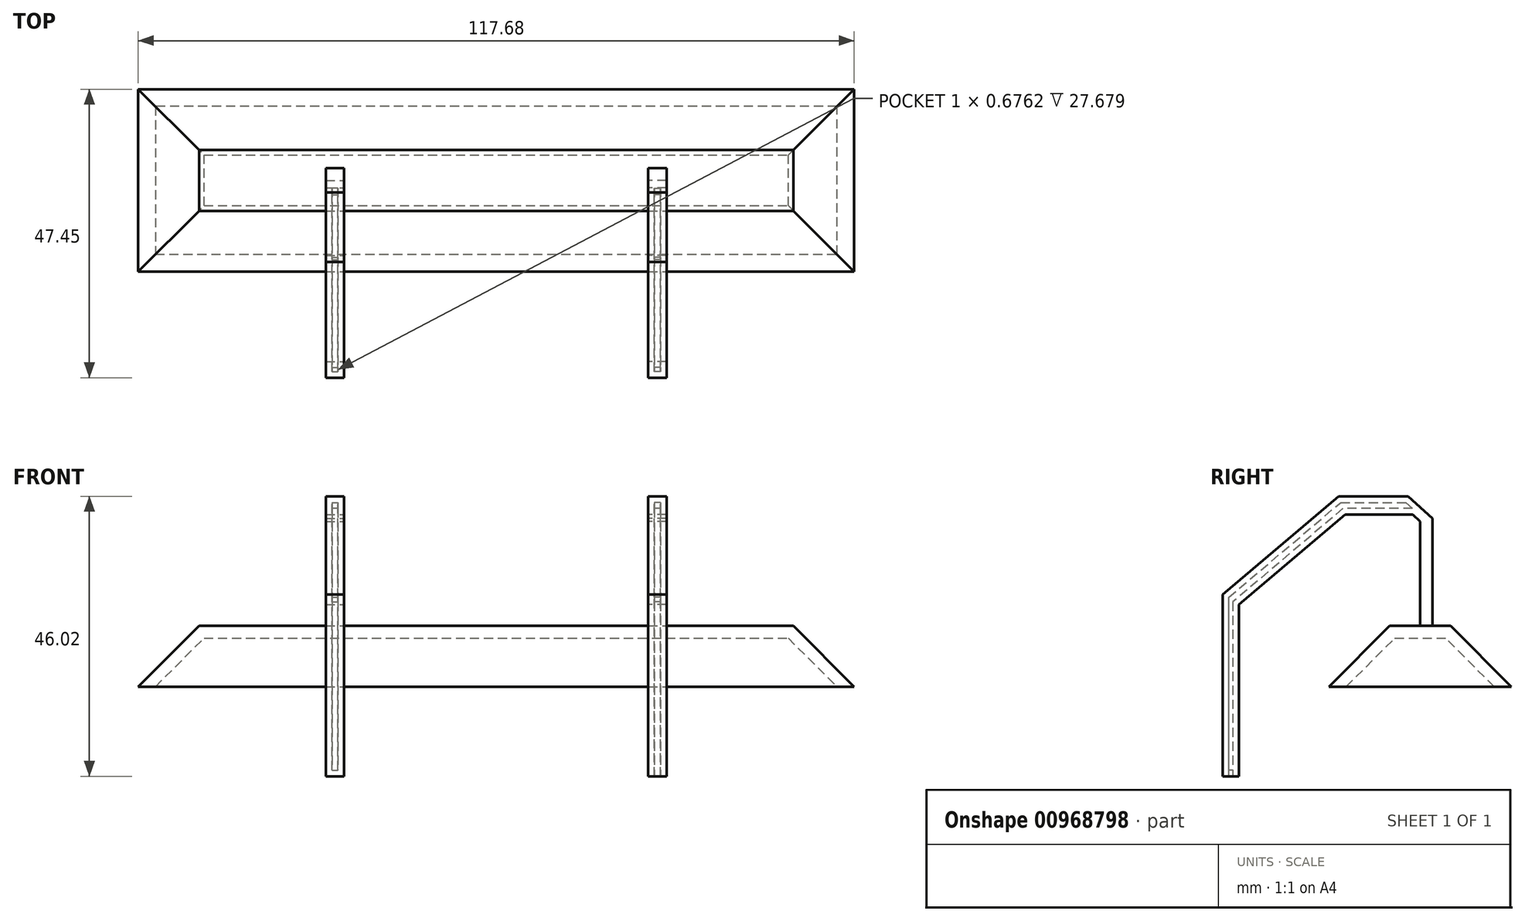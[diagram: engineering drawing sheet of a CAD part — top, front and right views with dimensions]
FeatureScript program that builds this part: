
annotation { "Feature Type Name" : "Feature", "Feature Type Description" : "" }
export const myFeature = defineFeature(function(context is Context, id is Id, definition is map)
    precondition{}
    {
        {
            var Q0;
            Q0=qCreatedBy(makeId("Top.planeOp"),FACE);
            var sketch = newSketch(context, id + "F0", { "sketchPlane" : qUnion([Q0])});
            skLineSegment(sketch, "E0.bottom", {"start": v(-0.04, 0) * mm, "end": v(117.64, 0) * mm});
            skLineSegment(sketch, "E0.top", {"start": v(-0.04, 30) * mm, "end": v(117.64, 30) * mm});
            skLineSegment(sketch, "E0.left", {"start": v(-0.04, 0) * mm, "end": v(-0.04, 30) * mm});
            skLineSegment(sketch, "E0.right", {"start": v(117.64, 0) * mm, "end": v(117.64, 30) * mm});
            skSolve(sketch);
        }
        {
            var Q0;
            Q0 = qSketchRegion(id + "F0", true);
            extrude(context, id + "F1", {"entities" : qUnion([Q0]), "depth" : 10 * mm, "offsetDistance" : 25 * mm});
        }
        {
            var Q0;
            Q0=makeQuery(id+"F1.opExtrude","CAP_EDGE",EDGE,{"disambiguationData":[OSD([sQuery(id+"F0.wireOp",EDGE,"E0.bottom")])],"isStart":false});
            var Q1;
            Q1=makeQuery(id+"F1.opExtrude","CAP_EDGE",EDGE,{"disambiguationData":[OSD([sQuery(id+"F0.wireOp",EDGE,"E0.right")])],"isStart":false});
            var Q2;
            Q2=makeQuery(id+"F1.opExtrude","CAP_EDGE",EDGE,{"disambiguationData":[OSD([sQuery(id+"F0.wireOp",EDGE,"E0.top")])],"isStart":false});
            var Q3;
            Q3=makeQuery(id+"F1.opExtrude","CAP_EDGE",EDGE,{"disambiguationData":[OSD([sQuery(id+"F0.wireOp",EDGE,"E0.left")])],"isStart":false});
            chamfer(context, id + "F2", {"entities" : qUnion([Q0, Q1, Q2, Q3]), "width" : 10 * mm, "tangentPropagation" : true});
        }
        {
            var Q0;
            Q0=makeQuery(id+"F1.opExtrude","CAP_FACE",FACE,{"disambiguationData":[OSD([sQuery(id+"F0.wireOp",EDGE,"E0.bottom"),sQuery(id+"F0.wireOp",EDGE,"E0.top"),sQuery(id+"F0.wireOp",EDGE,"E0.left"),sQuery(id+"F0.wireOp",EDGE,"E0.right")])],"isStart":true});
            shell(context, id + "F3", {"entities" : qUnion([Q0]), "thickness" : 2 * mm});
        }
        {
            var Q0;
            {var subQ0=sQuery(id+"F0.wireOp",EDGE,"E0.top");Q0=makeQuery(id+"F2.opChamfer","BLEND_EDGE",EDGE,{"blendedFrom":[makeQuery(id+"F1.opExtrude","CAP_EDGE",EDGE,{"disambiguationData":[OSD([subQ0])],"isStart":false}),makeQuery(id+"F1.opExtrude","CAP_FACE",FACE,{"disambiguationData":[OSD([sQuery(id+"F0.wireOp",EDGE,"E0.bottom"),subQ0,sQuery(id+"F0.wireOp",EDGE,"E0.left"),sQuery(id+"F0.wireOp",EDGE,"E0.right")])],"isStart":false})],"blendedInto":[makeQuery(id+"F1.opExtrude","CAP_FACE",FACE,{"disambiguationData":[OSD([sQuery(id+"F0.wireOp",EDGE,"E0.bottom"),subQ0,sQuery(id+"F0.wireOp",EDGE,"E0.left"),sQuery(id+"F0.wireOp",EDGE,"E0.right")])],"isStart":false})]});}
            cPoint(context, id + "F4", {"entities" : qUnion([Q0]), "parameter" : 0.5});
        }
        {
            var Q0;
            Q0=qCreatedBy(makeId("Right.planeOp"),FACE);
            var Q1;
            Q1 = qCreatedBy(id + "F4" ,VERTEX);
            cPlane(context, id + "F5", {"entities" : qUnion([Q0, Q1]), "cplaneType" : CPlaneType.PLANE_POINT, "offset" : 25 * mm, "oppositeDirection" : true, "flipAlignment" : true, "width" : 150 * mm, "height" : 150 * mm});
        }
        {
            var Q0;
            Q0=qCreatedBy(id+"F5.planeOp",FACE);
            cPlane(context, id + "F6", {"entities" : qUnion([Q0]), "cplaneType" : CPlaneType.OFFSET, "offset" : 25 * mm, "width" : 150 * mm, "height" : 150 * mm});
        }
        {
            var Q0;
            Q0=qCreatedBy(id+"F6.planeOp",FACE);
            var sketch = newSketch(context, id + "F7", { "sketchPlane" : qUnion([Q0])});
            skLineSegment(sketch, "E1.0.1", {"start": v(20, 10) * mm, "end": v(10, 10) * mm});
            skLineSegment(sketch, "E1.0.3", {"start": v(10, 10) * mm, "end": v(20, 10) * mm});
            skLineSegment(sketch, "E2", {"start": v(15.02, 10) * mm, "end": v(15.02, 27.17) * mm});
            skLineSegment(sketch, "E3", {"start": v(15.02, 27.17) * mm, "end": v(13.77, 28.3) * mm});
            skLineSegment(sketch, "E4", {"start": v(13.77, 28.3) * mm, "end": v(2.7, 28.3) * mm});
            skLineSegment(sketch, "E5", {"start": v(2.7, 28.3) * mm, "end": v(-14.78, 13.5) * mm});
            skLineSegment(sketch, "E6", {"start": v(-14.78, 13.5) * mm, "end": v(-14.78, -14.7) * mm});
            skLineSegment(sketch, "E7", {"start": v(-14.78, -14.7) * mm, "end": v(-17.45, -14.7) * mm});
            skLineSegment(sketch, "E8", {"start": v(-17.45, -14.7) * mm, "end": v(-17.45, 15.17) * mm});
            skLineSegment(sketch, "E9", {"start": v(-17.45, 15.17) * mm, "end": v(1.6, 31.3) * mm});
            skLineSegment(sketch, "E10", {"start": v(1.6, 31.3) * mm, "end": v(13.03, 31.3) * mm});
            skLineSegment(sketch, "E11", {"start": v(13.03, 31.3) * mm, "end": v(17.01, 27.68) * mm});
            skLineSegment(sketch, "E12", {"start": v(17.01, 27.68) * mm, "end": v(17.01, 10) * mm});
            skSolve(sketch);
        }
        {
            var Q0;
            Q0 = qSketchRegion(id + "F7", true);
            extrude(context, id + "F8", {"entities" : qUnion([Q0]), "depth" : 3 * mm, "offsetDistance" : 25 * mm});
        }
        {
            var Q0;
            Q0=makeQuery(id+"F8.opExtrude","SWEPT_BODY",BODY,{"disambiguationData":[OSD([sQuery(id+"F7.wireOp",EDGE,"E1.0.3"),sQuery(id+"F7.wireOp",EDGE,"E2"),sQuery(id+"F7.wireOp",EDGE,"E3"),sQuery(id+"F7.wireOp",EDGE,"E4"),sQuery(id+"F7.wireOp",EDGE,"E5"),sQuery(id+"F7.wireOp",EDGE,"E6"),sQuery(id+"F7.wireOp",EDGE,"E7"),sQuery(id+"F7.wireOp",EDGE,"E8"),sQuery(id+"F7.wireOp",EDGE,"E9"),sQuery(id+"F7.wireOp",EDGE,"E10"),sQuery(id+"F7.wireOp",EDGE,"E11"),sQuery(id+"F7.wireOp",EDGE,"E12")])]});
            var Q1;
            Q1=qCreatedBy(id+"F5.planeOp",FACE);
            mirror(context, id + "F9", {"operationType" : NewBodyOperationType.ADD, "entities" : qUnion([Q0]), "mirrorPlane" : qUnion([Q1])});
        }
        {
            var Q0;
            Q0=makeQuery(id+"F8.opExtrude","SWEPT_FACE",FACE,{"disambiguationData":[OSD([sQuery(id+"F7.wireOp",EDGE,"E7")])]});
            shell(context, id + "F10", {"entities" : qUnion([Q0]), "thickness" : 1 * mm});
        }
    });
